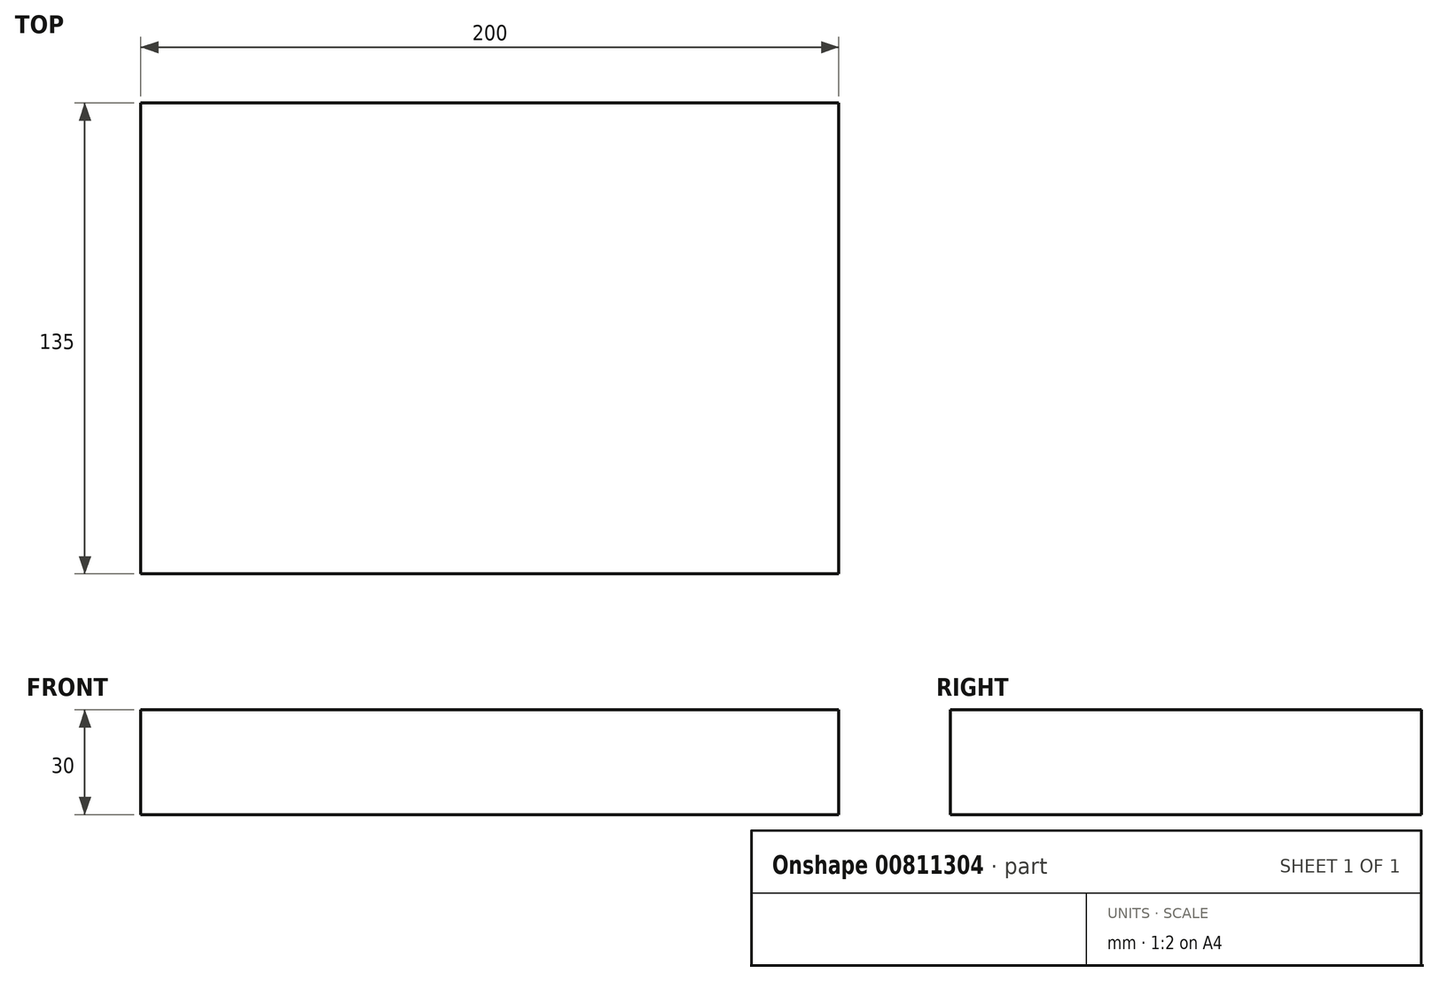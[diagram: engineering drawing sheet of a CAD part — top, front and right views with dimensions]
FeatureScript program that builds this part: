
annotation { "Feature Type Name" : "Feature", "Feature Type Description" : "" }
export const myFeature = defineFeature(function(context is Context, id is Id, definition is map)
    precondition{}
    {
        {
            var Q0;
            Q0=qCreatedBy(makeId("Top.planeOp"),FACE);
            var sketch = newSketch(context, id + "F0", { "sketchPlane" : qUnion([Q0])});
            skLineSegment(sketch, "E0.bottom", {"start": v(-88.64, 72.93) * mm, "end": v(111.36, 72.93) * mm});
            skLineSegment(sketch, "E0.top", {"start": v(-88.64, -62.07) * mm, "end": v(111.36, -62.07) * mm});
            skLineSegment(sketch, "E0.left", {"start": v(-88.64, 72.93) * mm, "end": v(-88.64, -62.07) * mm});
            skLineSegment(sketch, "E0.right", {"start": v(111.36, 72.93) * mm, "end": v(111.36, -62.07) * mm});
            skSolve(sketch);
        }
        {
            var Q0;
            Q0 = qSketchRegion(id + "F0", true);
            extrude(context, id + "F1", {"entities" : qUnion([Q0]), "depth" : 30 * mm, "offsetDistance" : 25 * mm});
        }
    });
